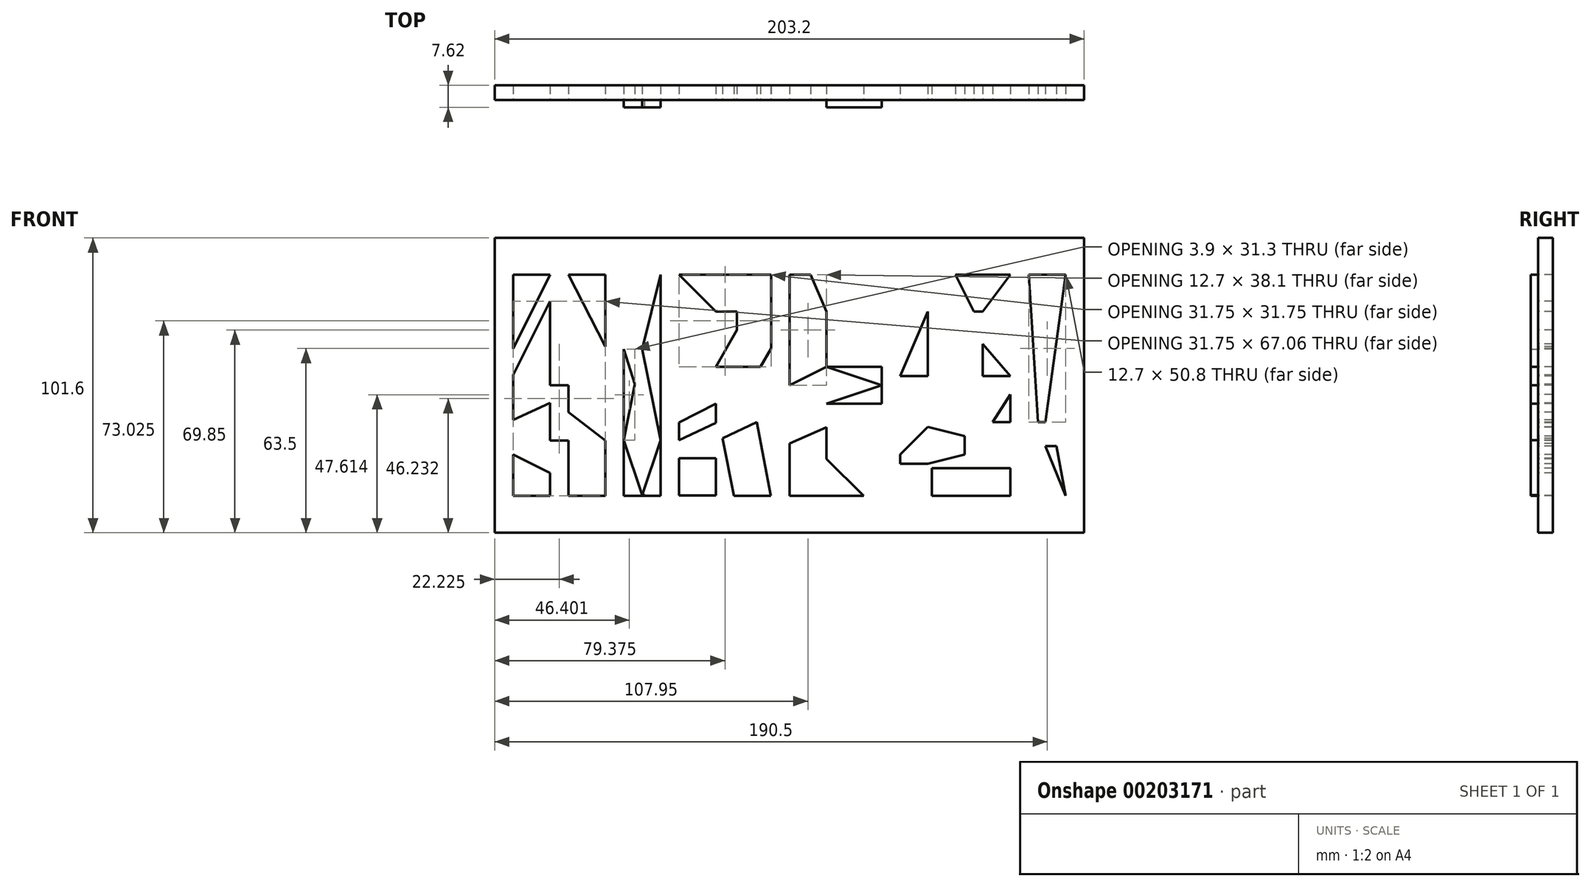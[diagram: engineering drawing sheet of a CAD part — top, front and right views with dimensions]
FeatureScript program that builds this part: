
annotation { "Feature Type Name" : "Feature", "Feature Type Description" : "" }
export const myFeature = defineFeature(function(context is Context, id is Id, definition is map)
    precondition{}
    {
        {
            var Q0;
            Q0=qCreatedBy(makeId("Front.planeOp"),FACE);
            var sketch = newSketch(context, id + "F0", { "sketchPlane" : qUnion([Q0])});
            skLineSegment(sketch, "E0.bottom", {"start": v(0, 0) * mm, "end": v(220.66, 0) * mm, "construction": true});
            skLineSegment(sketch, "E0.top", {"start": v(0, 138.11) * mm, "end": v(220.66, 138.11) * mm, "construction": true});
            skLineSegment(sketch, "E0.left", {"start": v(0, 0) * mm, "end": v(0, 138.11) * mm, "construction": true});
            skLineSegment(sketch, "E0.right", {"start": v(220.66, 0) * mm, "end": v(220.66, 138.11) * mm, "construction": true});
            skSolve(sketch);
        }
        {
            var Q0;
            Q0=qCreatedBy(makeId("Front.planeOp"),FACE);
            var sketch = newSketch(context, id + "F1", { "sketchPlane" : qUnion([Q0])});
            skLineSegment(sketch, "E1.bottom", {"start": v(0, 0) * mm, "end": v(203.2, 0) * mm});
            skLineSegment(sketch, "E1.top", {"start": v(0, 101.6) * mm, "end": v(203.2, 101.6) * mm});
            skLineSegment(sketch, "E1.left", {"start": v(0, 0) * mm, "end": v(0, 101.6) * mm});
            skLineSegment(sketch, "E1.right", {"start": v(203.2, 0) * mm, "end": v(203.2, 101.6) * mm});
            skSolve(sketch);
        }
        {
            var Q0;
            Q0=makeQuery(id+"F1.imprint","IMPRINT",FACE,{"disambiguationData":[TD([[makeQuery(id+"F1.imprint","IMPRINT",EDGE,{"derivedFrom":sQuery(id+"F1.wireOp",EDGE,"E1.bottom")}),1.0]])]});
            extrude(context, id + "F2", {"entities" : qUnion([Q0]), "oppositeDirection" : true, "depth" : 5.08 * mm});
        }
        {
            var Q0;
            Q0=makeQuery(id+"F2.opExtrude","CAP_FACE",FACE,{"disambiguationData":[OSD([sQuery(id+"F1.wireOp",EDGE,"E1.bottom"),sQuery(id+"F1.wireOp",EDGE,"E1.top"),sQuery(id+"F1.wireOp",EDGE,"E1.left"),sQuery(id+"F1.wireOp",EDGE,"E1.right")])],"isStart":true});
            var sketch = newSketch(context, id + "F3", { "sketchPlane" : qUnion([Q0])});
            skLineSegment(sketch, "E2", {"start": v(0, 50.8) * mm, "end": v(203.2, 50.8) * mm, "construction": true});
            skLineSegment(sketch, "E3", {"start": v(6.35, 88.9) * mm, "end": v(19.05, 88.9) * mm});
            skLineSegment(sketch, "E4", {"start": v(19.05, 88.9) * mm, "end": v(19.05, 50.8) * mm});
            skLineSegment(sketch, "E5", {"start": v(19.05, 50.8) * mm, "end": v(25.4, 50.8) * mm});
            skLineSegment(sketch, "E6", {"start": v(25.4, 50.8) * mm, "end": v(25.4, 88.9) * mm});
            skLineSegment(sketch, "E7", {"start": v(25.4, 88.9) * mm, "end": v(38.1, 88.9) * mm});
            skLineSegment(sketch, "E8", {"start": v(38.1, 88.9) * mm, "end": v(38.1, 50.8) * mm});
            skLineSegment(sketch, "E9", {"start": v(38.1, 50.8) * mm, "end": v(38.1, 12.7) * mm});
            skLineSegment(sketch, "E10", {"start": v(38.1, 12.7) * mm, "end": v(25.4, 12.7) * mm});
            skLineSegment(sketch, "E11", {"start": v(25.4, 12.7) * mm, "end": v(25.4, 31.75) * mm});
            skLineSegment(sketch, "E12", {"start": v(25.4, 31.75) * mm, "end": v(19.05, 31.75) * mm});
            skLineSegment(sketch, "E13", {"start": v(19.05, 31.75) * mm, "end": v(19.05, 12.7) * mm});
            skLineSegment(sketch, "E14", {"start": v(19.05, 12.7) * mm, "end": v(6.35, 12.7) * mm});
            skLineSegment(sketch, "E15", {"start": v(44.45, 88.9) * mm, "end": v(44.45, 12.7) * mm});
            skLineSegment(sketch, "E16", {"start": v(44.45, 12.7) * mm, "end": v(57.15, 12.7) * mm});
            skLineSegment(sketch, "E17", {"start": v(57.15, 12.7) * mm, "end": v(57.15, 88.9) * mm});
            skLineSegment(sketch, "E18", {"start": v(57.15, 88.9) * mm, "end": v(44.45, 88.9) * mm});
            skLineSegment(sketch, "E19", {"start": v(63.5, 88.9) * mm, "end": v(63.5, 12.7) * mm});
            skPoint(sketch, "E19.startSnap0", {"position": v(50.8, 88.9) * mm});
            skLineSegment(sketch, "E20", {"start": v(63.5, 12.7) * mm, "end": v(76.2, 12.7) * mm});
            skLineSegment(sketch, "E21", {"start": v(76.2, 12.7) * mm, "end": v(76.2, 44.45) * mm});
            skLineSegment(sketch, "E22", {"start": v(76.2, 44.45) * mm, "end": v(82.32, 12.7) * mm});
            skLineSegment(sketch, "E23", {"start": v(82.32, 12.7) * mm, "end": v(95.25, 12.7) * mm});
            skLineSegment(sketch, "E24", {"start": v(95.25, 12.7) * mm, "end": v(87.91, 50.8) * mm});
            skLineSegment(sketch, "E25", {"start": v(87.91, 50.8) * mm, "end": v(95.25, 63.5) * mm});
            skLineSegment(sketch, "E26", {"start": v(95.25, 63.5) * mm, "end": v(95.25, 88.9) * mm});
            skLineSegment(sketch, "E27", {"start": v(95.25, 88.9) * mm, "end": v(63.5, 88.9) * mm});
            skLineSegment(sketch, "E28", {"start": v(101.6, 88.9) * mm, "end": v(101.6, 12.7) * mm});
            skLineSegment(sketch, "E29", {"start": v(101.6, 12.7) * mm, "end": v(133.35, 12.7) * mm});
            skLineSegment(sketch, "E30", {"start": v(133.35, 12.7) * mm, "end": v(133.35, 25.4) * mm});
            skLineSegment(sketch, "E31", {"start": v(133.35, 25.4) * mm, "end": v(114.3, 25.4) * mm});
            skLineSegment(sketch, "E32", {"start": v(114.3, 25.4) * mm, "end": v(114.3, 44.45) * mm});
            skLineSegment(sketch, "E33", {"start": v(114.3, 44.45) * mm, "end": v(133.35, 44.45) * mm});
            skLineSegment(sketch, "E34", {"start": v(133.35, 44.45) * mm, "end": v(133.35, 57.15) * mm});
            skLineSegment(sketch, "E35", {"start": v(133.35, 57.15) * mm, "end": v(114.3, 57.15) * mm});
            skLineSegment(sketch, "E36", {"start": v(114.3, 57.15) * mm, "end": v(114.3, 76.2) * mm});
            skLineSegment(sketch, "E37", {"start": v(114.3, 76.2) * mm, "end": v(133.35, 76.2) * mm});
            skLineSegment(sketch, "E38", {"start": v(133.35, 76.2) * mm, "end": v(133.35, 88.9) * mm});
            skLineSegment(sketch, "E39", {"start": v(133.35, 88.9) * mm, "end": v(101.6, 88.9) * mm});
            skLineSegment(sketch, "E40", {"start": v(139.7, 88.9) * mm, "end": v(177.8, 88.9) * mm});
            skLineSegment(sketch, "E41", {"start": v(177.8, 88.9) * mm, "end": v(177.8, 53.98) * mm});
            skLineSegment(sketch, "E42", {"start": v(168.28, 53.98) * mm, "end": v(168.28, 76.2) * mm});
            skLineSegment(sketch, "E43", {"start": v(149.23, 76.2) * mm, "end": v(149.23, 53.98) * mm});
            skLineSegment(sketch, "E44", {"start": v(139.7, 12.7) * mm, "end": v(177.8, 12.7) * mm});
            skLineSegment(sketch, "E45", {"start": v(177.8, 12.7) * mm, "end": v(177.8, 22.23) * mm});
            skLineSegment(sketch, "E46", {"start": v(177.8, 22.23) * mm, "end": v(149.23, 22.23) * mm});
            skLineSegment(sketch, "E47", {"start": v(149.23, 22.23) * mm, "end": v(149.23, 23.81) * mm});
            skLineSegment(sketch, "E48", {"start": v(149.23, 36.51) * mm, "end": v(149.23, 38.1) * mm});
            skLineSegment(sketch, "E49", {"start": v(149.23, 38.1) * mm, "end": v(177.8, 38.1) * mm});
            skLineSegment(sketch, "E50", {"start": v(177.8, 38.1) * mm, "end": v(177.8, 47.63) * mm});
            skLineSegment(sketch, "E51", {"start": v(6.35, 88.9) * mm, "end": v(6.35, 12.7) * mm});
            skLineSegment(sketch, "E52", {"start": v(149.23, 76.2) * mm, "end": v(152.4, 76.2) * mm});
            skLineSegment(sketch, "E53", {"start": v(152.4, 76.2) * mm, "end": v(155.57, 63.5) * mm});
            skLineSegment(sketch, "E54", {"start": v(155.57, 63.5) * mm, "end": v(161.93, 63.5) * mm});
            skLineSegment(sketch, "E55", {"start": v(161.93, 63.5) * mm, "end": v(165.1, 76.2) * mm});
            skLineSegment(sketch, "E56", {"start": v(165.1, 76.2) * mm, "end": v(168.28, 76.2) * mm});
            skPoint(sketch, "E57", {"position": v(158.75, 88.9) * mm});
            skPoint(sketch, "E58", {"position": v(158.75, 63.5) * mm});
            skLineSegment(sketch, "E59", {"start": v(161.93, 33.34) * mm, "end": v(161.93, 26.99) * mm});
            skPoint(sketch, "E60", {"position": v(161.93, 30.16) * mm});
            skLineSegment(sketch, "E61", {"start": v(139.7, 88.9) * mm, "end": v(139.7, 53.98) * mm});
            skLineSegment(sketch, "E62", {"start": v(139.7, 53.98) * mm, "end": v(149.23, 53.98) * mm});
            skLineSegment(sketch, "E63", {"start": v(168.28, 53.98) * mm, "end": v(177.8, 53.98) * mm});
            skLineSegment(sketch, "E64", {"start": v(139.7, 47.63) * mm, "end": v(177.8, 47.63) * mm});
            skLineSegment(sketch, "E65", {"start": v(139.7, 47.63) * mm, "end": v(139.7, 12.7) * mm});
            skLineSegment(sketch, "E66", {"start": v(161.93, 33.34) * mm, "end": v(149.23, 36.51) * mm});
            skLineSegment(sketch, "E67", {"start": v(149.23, 23.81) * mm, "end": v(161.93, 26.99) * mm});
            skPoint(sketch, "E68", {"position": v(139.7, 30.16) * mm});
            skLineSegment(sketch, "E69", {"start": v(184.15, 88.9) * mm, "end": v(196.85, 88.9) * mm});
            skLineSegment(sketch, "E70", {"start": v(196.85, 88.9) * mm, "end": v(193.67, 38.1) * mm});
            skLineSegment(sketch, "E71", {"start": v(193.67, 38.1) * mm, "end": v(187.33, 38.1) * mm});
            skLineSegment(sketch, "E72", {"start": v(187.33, 38.1) * mm, "end": v(184.15, 88.9) * mm});
            skPoint(sketch, "E73", {"position": v(190.5, 88.9) * mm});
            skPoint(sketch, "E74", {"position": v(190.5, 38.1) * mm});
            skLineSegment(sketch, "E75", {"start": v(187.32, 29.85) * mm, "end": v(184.15, 12.7) * mm});
            skLineSegment(sketch, "E76", {"start": v(184.15, 12.7) * mm, "end": v(196.85, 12.7) * mm});
            skLineSegment(sketch, "E77", {"start": v(196.85, 12.7) * mm, "end": v(193.68, 29.85) * mm});
            skLineSegment(sketch, "E78", {"start": v(193.67, 29.85) * mm, "end": v(187.33, 29.85) * mm});
            skPoint(sketch, "E79", {"position": v(190.5, 29.85) * mm});
            skPoint(sketch, "E80", {"position": v(190.5, 12.7) * mm});
            skLineSegment(sketch, "E81", {"start": v(76.2, 57.15) * mm, "end": v(76.2, 76.2) * mm});
            skLineSegment(sketch, "E82", {"start": v(76.2, 76.2) * mm, "end": v(83.54, 76.2) * mm});
            skLineSegment(sketch, "E83", {"start": v(83.54, 76.2) * mm, "end": v(83.54, 69.85) * mm});
            skLineSegment(sketch, "E84", {"start": v(83.54, 69.85) * mm, "end": v(76.2, 57.15) * mm});
            skSolve(sketch);
        }
        {
            var Q0;
            Q0=makeQuery(id+"F3.imprint","IMPRINT",FACE,{"disambiguationData":[TD([[makeQuery(id+"F3.imprint","IMPRINT",EDGE,{"derivedFrom":sQuery(id+"F3.wireOp",EDGE,"E3")}),1.0]])]});
            var sketch = newSketch(context, id + "F4", { "sketchPlane" : qUnion([Q0])});
            skLineSegment(sketch, "E85", {"start": v(6.35, 63.49) * mm, "end": v(19.05, 88.9) * mm});
            skLineSegment(sketch, "E86", {"start": v(19.05, 88.9) * mm, "end": v(6.35, 88.9) * mm});
            skLineSegment(sketch, "E87", {"start": v(6.35, 88.9) * mm, "end": v(6.35, 63.49) * mm});
            skLineSegment(sketch, "E88", {"start": v(6.35, 54.35) * mm, "end": v(19.05, 79.76) * mm});
            skLineSegment(sketch, "E89", {"start": v(19.05, 79.76) * mm, "end": v(19.05, 50.8) * mm});
            skLineSegment(sketch, "E90", {"start": v(6.35, 38.97) * mm, "end": v(6.35, 54.35) * mm});
            skLineSegment(sketch, "E91", {"start": v(19.05, 31.75) * mm, "end": v(19.05, 44.79) * mm});
            skLineSegment(sketch, "E92", {"start": v(25.4, 41.55) * mm, "end": v(38.1, 31.75) * mm});
            skLineSegment(sketch, "E93", {"start": v(6.35, 26.94) * mm, "end": v(19.05, 20.6) * mm});
            skLineSegment(sketch, "E94", {"start": v(19.05, 20.6) * mm, "end": v(19.05, 12.7) * mm});
            skLineSegment(sketch, "E95", {"start": v(19.05, 12.7) * mm, "end": v(6.35, 12.7) * mm});
            skLineSegment(sketch, "E96", {"start": v(6.35, 12.7) * mm, "end": v(6.35, 26.94) * mm});
            skLineSegment(sketch, "E97", {"start": v(19.05, 50.8) * mm, "end": v(25.4, 50.8) * mm});
            skLineSegment(sketch, "E98", {"start": v(25.4, 50.8) * mm, "end": v(25.4, 41.55) * mm});
            skLineSegment(sketch, "E99", {"start": v(6.35, 38.97) * mm, "end": v(19.05, 44.79) * mm});
            skLineSegment(sketch, "E100", {"start": v(38.1, 31.75) * mm, "end": v(38.1, 12.7) * mm});
            skLineSegment(sketch, "E101", {"start": v(38.1, 12.7) * mm, "end": v(25.4, 12.7) * mm});
            skLineSegment(sketch, "E102", {"start": v(25.4, 12.7) * mm, "end": v(25.4, 31.75) * mm});
            skLineSegment(sketch, "E103", {"start": v(25.4, 31.75) * mm, "end": v(19.05, 31.75) * mm});
            skLineSegment(sketch, "E104", {"start": v(25.4, 64.16) * mm, "end": v(25.4, 88.9) * mm});
            skLineSegment(sketch, "E105", {"start": v(25.4, 88.9) * mm, "end": v(38.12, 64.16) * mm});
            skLineSegment(sketch, "E106", {"start": v(38.12, 64.16) * mm, "end": v(25.4, 64.16) * mm});
            skLineSegment(sketch, "E107", {"start": v(44.45, 88.9) * mm, "end": v(44.45, 63.26) * mm});
            skLineSegment(sketch, "E108", {"start": v(44.45, 63.26) * mm, "end": v(48.35, 51.2) * mm});
            skLineSegment(sketch, "E109", {"start": v(48.35, 51.2) * mm, "end": v(44.45, 31.96) * mm});
            skLineSegment(sketch, "E110", {"start": v(44.45, 31.96) * mm, "end": v(50.8, 12.7) * mm});
            skLineSegment(sketch, "E111", {"start": v(50.8, 12.7) * mm, "end": v(57.15, 31.96) * mm});
            skLineSegment(sketch, "E112", {"start": v(57.15, 31.96) * mm, "end": v(53.25, 51.2) * mm});
            skLineSegment(sketch, "E113", {"start": v(53.25, 51.2) * mm, "end": v(50.8, 63.26) * mm});
            skLineSegment(sketch, "E114", {"start": v(50.8, 63.26) * mm, "end": v(57.15, 88.9) * mm});
            skLineSegment(sketch, "E115", {"start": v(57.15, 88.9) * mm, "end": v(44.45, 88.9) * mm});
            skLineSegment(sketch, "E116", {"start": v(63.5, 88.9) * mm, "end": v(76.2, 76.2) * mm});
            skLineSegment(sketch, "E117", {"start": v(76.2, 76.2) * mm, "end": v(76.2, 57.15) * mm});
            skLineSegment(sketch, "E118", {"start": v(63.5, 38.08) * mm, "end": v(63.5, 88.9) * mm});
            skLineSegment(sketch, "E119", {"start": v(63.5, 25.77) * mm, "end": v(63.5, 31.96) * mm});
            skLineSegment(sketch, "E120", {"start": v(63.5, 31.96) * mm, "end": v(76.2, 37.86) * mm});
            skLineSegment(sketch, "E121", {"start": v(76.2, 37.86) * mm, "end": v(76.2, 25.77) * mm});
            skLineSegment(sketch, "E122", {"start": v(76.2, 25.77) * mm, "end": v(63.5, 25.77) * mm});
            skLineSegment(sketch, "E123", {"start": v(76.2, 57.15) * mm, "end": v(91.58, 57.15) * mm});
            skLineSegment(sketch, "E124", {"start": v(91.58, 57.15) * mm, "end": v(87.91, 50.8) * mm});
            skLineSegment(sketch, "E125", {"start": v(76.2, 44.45) * mm, "end": v(63.5, 38.08) * mm});
            skLineSegment(sketch, "E126", {"start": v(78.48, 32.6) * mm, "end": v(90.35, 38.12) * mm});
            skLineSegment(sketch, "E127", {"start": v(114.3, 57.15) * mm, "end": v(101.6, 50.8) * mm});
            skLineSegment(sketch, "E128", {"start": v(101.6, 50.8) * mm, "end": v(114.3, 44.45) * mm});
            skLineSegment(sketch, "E129", {"start": v(114.3, 44.45) * mm, "end": v(133.35, 50.8) * mm});
            skLineSegment(sketch, "E130", {"start": v(133.35, 50.8) * mm, "end": v(114.3, 57.15) * mm});
            skLineSegment(sketch, "E131", {"start": v(114.3, 36.42) * mm, "end": v(101.6, 30.85) * mm});
            skLineSegment(sketch, "E132", {"start": v(101.6, 30.85) * mm, "end": v(101.6, 12.7) * mm});
            skLineSegment(sketch, "E133", {"start": v(101.6, 12.7) * mm, "end": v(127.23, 12.7) * mm});
            skLineSegment(sketch, "E134", {"start": v(127.23, 12.7) * mm, "end": v(114.3, 25.4) * mm});
            skLineSegment(sketch, "E135", {"start": v(114.3, 25.4) * mm, "end": v(114.3, 36.42) * mm});
            skLineSegment(sketch, "E136", {"start": v(108.95, 88.9) * mm, "end": v(114.3, 76.2) * mm});
            skLineSegment(sketch, "E137", {"start": v(114.3, 76.2) * mm, "end": v(133.35, 76.2) * mm});
            skLineSegment(sketch, "E138", {"start": v(133.35, 76.2) * mm, "end": v(133.35, 88.9) * mm});
            skLineSegment(sketch, "E139", {"start": v(133.35, 88.9) * mm, "end": v(108.95, 88.9) * mm});
            skLineSegment(sketch, "E140", {"start": v(152.4, 76.2) * mm, "end": v(158.75, 88.9) * mm});
            skLineSegment(sketch, "E141", {"start": v(158.75, 88.9) * mm, "end": v(165.1, 76.2) * mm});
            skLineSegment(sketch, "E142", {"start": v(165.1, 76.2) * mm, "end": v(161.93, 63.5) * mm});
            skLineSegment(sketch, "E143", {"start": v(161.93, 63.5) * mm, "end": v(155.57, 63.5) * mm});
            skLineSegment(sketch, "E144", {"start": v(155.57, 63.5) * mm, "end": v(152.4, 76.2) * mm});
            skLineSegment(sketch, "E145", {"start": v(168.28, 76.2) * mm, "end": v(177.8, 88.9) * mm});
            skLineSegment(sketch, "E146", {"start": v(177.8, 88.9) * mm, "end": v(177.8, 53.98) * mm});
            skLineSegment(sketch, "E147", {"start": v(177.8, 53.97) * mm, "end": v(168.27, 65.09) * mm});
            skLineSegment(sketch, "E148", {"start": v(168.28, 65.09) * mm, "end": v(168.28, 76.2) * mm});
            skLineSegment(sketch, "E149", {"start": v(139.7, 53.98) * mm, "end": v(149.23, 53.98) * mm});
            skLineSegment(sketch, "E150", {"start": v(149.23, 53.98) * mm, "end": v(149.23, 76.2) * mm});
            skLineSegment(sketch, "E151", {"start": v(149.23, 76.2) * mm, "end": v(139.7, 53.98) * mm});
            skLineSegment(sketch, "E152", {"start": v(139.7, 47.63) * mm, "end": v(177.8, 47.63) * mm});
            skLineSegment(sketch, "E153", {"start": v(177.8, 47.63) * mm, "end": v(171.66, 38.1) * mm});
            skLineSegment(sketch, "E154", {"start": v(171.66, 38.1) * mm, "end": v(149.23, 38.1) * mm});
            skLineSegment(sketch, "E155", {"start": v(139.7, 47.63) * mm, "end": v(139.7, 26.99) * mm});
            skLineSegment(sketch, "E156", {"start": v(139.7, 26.99) * mm, "end": v(149.23, 36.51) * mm});
            skLineSegment(sketch, "E157", {"start": v(149.23, 36.51) * mm, "end": v(149.23, 38.1) * mm});
            skLineSegment(sketch, "E158", {"start": v(150.7, 22.23) * mm, "end": v(150.7, 12.7) * mm});
            skLineSegment(sketch, "E159", {"start": v(150.7, 12.7) * mm, "end": v(139.7, 12.7) * mm});
            skLineSegment(sketch, "E160", {"start": v(139.7, 12.7) * mm, "end": v(139.7, 23.81) * mm});
            skLineSegment(sketch, "E161", {"start": v(139.7, 23.81) * mm, "end": v(149.23, 23.81) * mm});
            skLineSegment(sketch, "E162", {"start": v(149.23, 23.81) * mm, "end": v(149.23, 22.23) * mm});
            skLineSegment(sketch, "E163", {"start": v(149.23, 22.23) * mm, "end": v(150.7, 22.23) * mm});
            skLineSegment(sketch, "E164", {"start": v(187.33, 38.1) * mm, "end": v(187.33, 88.9) * mm});
            skLineSegment(sketch, "E165", {"start": v(187.33, 88.9) * mm, "end": v(184.15, 88.9) * mm});
            skLineSegment(sketch, "E166", {"start": v(184.15, 88.9) * mm, "end": v(187.33, 38.1) * mm});
            skLineSegment(sketch, "E167", {"start": v(189.76, 29.85) * mm, "end": v(196.85, 12.7) * mm});
            skLineSegment(sketch, "E168", {"start": v(196.85, 12.7) * mm, "end": v(193.68, 29.85) * mm});
            skLineSegment(sketch, "E169", {"start": v(193.68, 29.85) * mm, "end": v(189.76, 29.85) * mm});
            skLineSegment(sketch, "E170", {"start": v(189.76, 38.1) * mm, "end": v(196.85, 88.9) * mm});
            skLineSegment(sketch, "E171", {"start": v(196.85, 88.9) * mm, "end": v(193.68, 38.1) * mm});
            skLineSegment(sketch, "E172", {"start": v(193.67, 38.1) * mm, "end": v(189.76, 38.1) * mm});
            skLineSegment(sketch, "E173", {"start": v(48.35, 51.2) * mm, "end": v(53.25, 51.2) * mm, "construction": true});
            skPoint(sketch, "E174", {"position": v(50.8, 51.2) * mm});
            skLineSegment(sketch, "E175", {"start": v(57.15, 88.9) * mm, "end": v(57.15, 31.96) * mm});
            skLineSegment(sketch, "E176", {"start": v(50.8, 12.7) * mm, "end": v(57.15, 12.7) * mm});
            skLineSegment(sketch, "E177", {"start": v(57.15, 12.7) * mm, "end": v(57.15, 31.96) * mm});
            skLineSegment(sketch, "E178", {"start": v(50.8, 12.7) * mm, "end": v(44.45, 12.7) * mm});
            skLineSegment(sketch, "E179", {"start": v(44.45, 12.7) * mm, "end": v(44.45, 31.96) * mm});
            skLineSegment(sketch, "E180", {"start": v(44.45, 63.26) * mm, "end": v(44.45, 31.96) * mm});
            skLineSegment(sketch, "E181", {"start": v(63.5, 88.9) * mm, "end": v(95.29, 88.9) * mm});
            skLineSegment(sketch, "E182", {"start": v(95.29, 88.9) * mm, "end": v(95.29, 63.17) * mm});
            skLineSegment(sketch, "E183", {"start": v(95.29, 63.17) * mm, "end": v(91.58, 57.15) * mm});
            skLineSegment(sketch, "E184", {"start": v(76.2, 57.15) * mm, "end": v(83.54, 69.85) * mm});
            skLineSegment(sketch, "E185", {"start": v(83.54, 69.85) * mm, "end": v(83.54, 76.2) * mm});
            skLineSegment(sketch, "E186", {"start": v(83.54, 76.2) * mm, "end": v(76.2, 76.2) * mm});
            skLineSegment(sketch, "E187", {"start": v(63.5, 38.08) * mm, "end": v(63.5, 31.96) * mm});
            skLineSegment(sketch, "E188", {"start": v(63.5, 25.77) * mm, "end": v(63.5, 12.87) * mm});
            skLineSegment(sketch, "E189", {"start": v(63.5, 12.87) * mm, "end": v(76.2, 12.87) * mm});
            skLineSegment(sketch, "E190", {"start": v(76.2, 12.87) * mm, "end": v(76.2, 25.77) * mm});
            skLineSegment(sketch, "E191", {"start": v(78.48, 32.6) * mm, "end": v(82.53, 12.66) * mm});
            skLineSegment(sketch, "E192", {"start": v(82.53, 12.66) * mm, "end": v(95.17, 12.66) * mm});
            skLineSegment(sketch, "E193", {"start": v(95.17, 12.66) * mm, "end": v(90.35, 38.12) * mm});
            skLineSegment(sketch, "E194", {"start": v(76.2, 44.45) * mm, "end": v(78.48, 32.6) * mm});
            skLineSegment(sketch, "E195", {"start": v(90.35, 38.12) * mm, "end": v(87.91, 50.8) * mm});
            skLineSegment(sketch, "E196", {"start": v(76.2, 37.86) * mm, "end": v(76.2, 44.45) * mm});
            skLineSegment(sketch, "E197", {"start": v(108.95, 88.9) * mm, "end": v(101.6, 88.9) * mm});
            skLineSegment(sketch, "E198", {"start": v(101.6, 88.9) * mm, "end": v(101.6, 50.8) * mm});
            skLineSegment(sketch, "E199", {"start": v(101.6, 50.8) * mm, "end": v(101.6, 30.85) * mm});
            skLineSegment(sketch, "E200", {"start": v(114.3, 36.42) * mm, "end": v(114.3, 44.45) * mm});
            skLineSegment(sketch, "E201", {"start": v(114.3, 44.45) * mm, "end": v(133.35, 44.45) * mm});
            skLineSegment(sketch, "E202", {"start": v(133.35, 44.45) * mm, "end": v(133.35, 50.8) * mm});
            skLineSegment(sketch, "E203", {"start": v(133.35, 50.8) * mm, "end": v(133.35, 57.15) * mm});
            skLineSegment(sketch, "E204", {"start": v(133.35, 57.15) * mm, "end": v(114.3, 57.15) * mm});
            skLineSegment(sketch, "E205", {"start": v(114.3, 57.15) * mm, "end": v(114.3, 76.2) * mm});
            skLineSegment(sketch, "E206", {"start": v(114.3, 25.4) * mm, "end": v(133.35, 25.4) * mm});
            skLineSegment(sketch, "E207", {"start": v(133.35, 25.4) * mm, "end": v(133.35, 12.76) * mm});
            skLineSegment(sketch, "E208", {"start": v(133.35, 12.76) * mm, "end": v(127.23, 12.7) * mm});
            skLineSegment(sketch, "E209", {"start": v(150.7, 12.7) * mm, "end": v(177.8, 12.7) * mm});
            skLineSegment(sketch, "E210", {"start": v(177.8, 12.7) * mm, "end": v(177.8, 22.23) * mm});
            skLineSegment(sketch, "E211", {"start": v(177.8, 22.23) * mm, "end": v(150.7, 22.23) * mm});
            skLineSegment(sketch, "E212", {"start": v(149.23, 23.81) * mm, "end": v(161.93, 26.99) * mm});
            skLineSegment(sketch, "E213", {"start": v(161.93, 33.34) * mm, "end": v(149.23, 36.51) * mm});
            skLineSegment(sketch, "E214", {"start": v(139.7, 23.81) * mm, "end": v(139.7, 26.99) * mm});
            skLineSegment(sketch, "E215", {"start": v(171.66, 38.1) * mm, "end": v(177.8, 38.1) * mm});
            skLineSegment(sketch, "E216", {"start": v(177.8, 38.1) * mm, "end": v(177.8, 47.63) * mm});
            skLineSegment(sketch, "E217", {"start": v(139.7, 53.98) * mm, "end": v(139.7, 88.9) * mm});
            skLineSegment(sketch, "E218", {"start": v(139.7, 88.9) * mm, "end": v(158.75, 88.9) * mm});
            skLineSegment(sketch, "E219", {"start": v(149.22, 76.2) * mm, "end": v(149.22, 76.2) * mm});
            skLineSegment(sketch, "E220", {"start": v(149.23, 76.2) * mm, "end": v(152.4, 76.2) * mm});
            skLineSegment(sketch, "E221", {"start": v(158.75, 88.9) * mm, "end": v(177.8, 88.9) * mm});
            skLineSegment(sketch, "E222", {"start": v(168.28, 76.2) * mm, "end": v(165.1, 76.2) * mm});
            skLineSegment(sketch, "E223", {"start": v(168.28, 65.09) * mm, "end": v(168.28, 53.98) * mm});
            skLineSegment(sketch, "E224", {"start": v(168.28, 53.98) * mm, "end": v(177.8, 53.98) * mm});
            skLineSegment(sketch, "E225", {"start": v(187.33, 88.9) * mm, "end": v(196.85, 88.9) * mm});
            skLineSegment(sketch, "E226", {"start": v(189.76, 38.1) * mm, "end": v(187.33, 38.1) * mm});
            skLineSegment(sketch, "E227", {"start": v(189.76, 29.85) * mm, "end": v(187.33, 29.85) * mm});
            skLineSegment(sketch, "E228", {"start": v(187.33, 29.85) * mm, "end": v(184.3, 12.7) * mm});
            skLineSegment(sketch, "E229", {"start": v(184.3, 12.7) * mm, "end": v(196.85, 12.7) * mm});
            skLineSegment(sketch, "E230", {"start": v(161.93, 26.99) * mm, "end": v(161.93, 33.34) * mm});
            skLineSegment(sketch, "E231", {"start": v(19.05, 20.6) * mm, "end": v(19.05, 31.75) * mm});
            skLineSegment(sketch, "E232", {"start": v(6.35, 38.97) * mm, "end": v(6.35, 26.94) * mm});
            skLineSegment(sketch, "E233", {"start": v(6.35, 54.35) * mm, "end": v(6.35, 63.49) * mm});
            skLineSegment(sketch, "E234", {"start": v(25.4, 88.9) * mm, "end": v(38.1, 88.9) * mm});
            skLineSegment(sketch, "E235", {"start": v(38.1, 88.9) * mm, "end": v(38.12, 64.16) * mm});
            skLineSegment(sketch, "E236", {"start": v(38.1, 31.75) * mm, "end": v(38.12, 64.16) * mm});
            skLineSegment(sketch, "E237", {"start": v(25.4, 50.8) * mm, "end": v(25.4, 64.16) * mm});
            skLineSegment(sketch, "E238", {"start": v(44.45, 31.96) * mm, "end": v(44.45, 12.7) * mm});
            skLineSegment(sketch, "E239", {"start": v(57.15, 31.96) * mm, "end": v(57.15, 12.7) * mm});
            skSolve(sketch);
        }
        {
            var Q0;
            {var subQ29=sQuery(id+"F4.wireOp",EDGE,"E86");Q0=makeQuery(id+"F4.imprint","IMPRINT",FACE,{"disambiguationData":[TD([[makeQuery(id+"F4.imprint","IMPRINT",EDGE,{"derivedFrom":subQ29}),1.0]])]});}
            var sketch = newSketch(context, id + "F5", { "sketchPlane" : qUnion([Q0])});
            skLineSegment(sketch, "E240", {"start": v(108.95, 88.9) * mm, "end": v(133.35, 88.9) * mm});
            skLineSegment(sketch, "E241", {"start": v(133.35, 88.9) * mm, "end": v(133.35, 76.2) * mm});
            skLineSegment(sketch, "E242", {"start": v(133.35, 76.2) * mm, "end": v(114.3, 76.2) * mm});
            skLineSegment(sketch, "E243", {"start": v(114.3, 76.2) * mm, "end": v(108.95, 88.9) * mm});
            skLineSegment(sketch, "E244", {"start": v(114.3, 57.15) * mm, "end": v(133.35, 50.8) * mm});
            skLineSegment(sketch, "E245", {"start": v(133.35, 50.8) * mm, "end": v(133.35, 57.15) * mm});
            skLineSegment(sketch, "E246", {"start": v(133.35, 57.15) * mm, "end": v(114.3, 57.15) * mm});
            skLineSegment(sketch, "E247", {"start": v(114.3, 44.45) * mm, "end": v(133.35, 44.45) * mm});
            skLineSegment(sketch, "E248", {"start": v(133.35, 44.45) * mm, "end": v(133.35, 50.8) * mm});
            skLineSegment(sketch, "E249", {"start": v(133.35, 50.8) * mm, "end": v(114.3, 44.45) * mm});
            skLineSegment(sketch, "E250", {"start": v(50.8, 63.26) * mm, "end": v(57.15, 88.9) * mm});
            skLineSegment(sketch, "E251", {"start": v(57.15, 88.9) * mm, "end": v(57.15, 31.96) * mm});
            skLineSegment(sketch, "E252", {"start": v(57.15, 31.96) * mm, "end": v(50.8, 63.26) * mm});
            skLineSegment(sketch, "E253", {"start": v(44.45, 12.7) * mm, "end": v(50.8, 12.7) * mm});
            skLineSegment(sketch, "E254", {"start": v(44.45, 31.96) * mm, "end": v(44.45, 12.7) * mm});
            skLineSegment(sketch, "E255", {"start": v(168.28, 65.09) * mm, "end": v(168.28, 53.98) * mm});
            skLineSegment(sketch, "E256", {"start": v(168.28, 53.98) * mm, "end": v(177.8, 53.98) * mm});
            skLineSegment(sketch, "E257", {"start": v(177.8, 53.97) * mm, "end": v(168.28, 65.09) * mm});
            skLineSegment(sketch, "E258", {"start": v(171.66, 38.1) * mm, "end": v(177.8, 38.1) * mm});
            skLineSegment(sketch, "E259", {"start": v(177.8, 38.1) * mm, "end": v(177.8, 47.63) * mm});
            skLineSegment(sketch, "E260", {"start": v(177.8, 47.63) * mm, "end": v(171.66, 38.1) * mm});
            skLineSegment(sketch, "E261", {"start": v(184.15, 88.9) * mm, "end": v(196.85, 88.9) * mm});
            skLineSegment(sketch, "E262", {"start": v(196.85, 88.9) * mm, "end": v(189.76, 38.1) * mm});
            skLineSegment(sketch, "E263", {"start": v(189.76, 38.1) * mm, "end": v(187.33, 38.1) * mm});
            skLineSegment(sketch, "E264", {"start": v(187.33, 38.1) * mm, "end": v(184.15, 88.9) * mm});
            skLineSegment(sketch, "E265", {"start": v(189.76, 29.84) * mm, "end": v(193.68, 29.85) * mm});
            skLineSegment(sketch, "E266", {"start": v(193.67, 29.85) * mm, "end": v(196.85, 12.7) * mm});
            skLineSegment(sketch, "E267", {"start": v(196.85, 12.7) * mm, "end": v(189.76, 29.85) * mm});
            skLineSegment(sketch, "E268", {"start": v(44.45, 31.96) * mm, "end": v(50.8, 12.95) * mm});
            skLineSegment(sketch, "E269", {"start": v(50.8, 12.95) * mm, "end": v(51.7, 12.95) * mm});
            skLineSegment(sketch, "E270", {"start": v(51.7, 12.95) * mm, "end": v(51.7, 12.7) * mm});
            skLineSegment(sketch, "E271", {"start": v(51.7, 12.7) * mm, "end": v(50.8, 12.7) * mm});
            skSolve(sketch);
        }
        {
            var Q0;
            Q0=makeQuery(id+"F4.imprint","IMPRINT",FACE,{"disambiguationData":[TD([[makeQuery(id+"F4.imprint","IMPRINT",EDGE,{"derivedFrom":sQuery(id+"F4.wireOp",EDGE,"E85")}),1.0]])]});
            var Q1;
            {var subQ0=sQuery(id+"F4.wireOp",EDGE,"E234");Q1=makeQuery(id+"F4.imprint","IMPRINT",FACE,{"disambiguationData":[TD([[makeQuery(id+"F4.imprint","IMPRINT",EDGE,{"derivedFrom":subQ0}),-1.0]])]});}
            var Q2;
            Q2=makeQuery(id+"F4.imprint","IMPRINT",FACE,{"disambiguationData":[TD([[makeQuery(id+"F4.imprint","IMPRINT",EDGE,{"derivedFrom":sQuery(id+"F4.wireOp",EDGE,"E88")}),-1.0]])]});
            var Q3;
            Q3=makeQuery(id+"F4.imprint","IMPRINT",FACE,{"disambiguationData":[TD([[makeQuery(id+"F4.imprint","IMPRINT",EDGE,{"derivedFrom":sQuery(id+"F4.wireOp",EDGE,"E93")}),-1.0]])]});
            var Q4;
            Q4=makeQuery(id+"F4.imprint","IMPRINT",FACE,{"disambiguationData":[TD([[makeQuery(id+"F4.imprint","IMPRINT",EDGE,{"derivedFrom":sQuery(id+"F4.wireOp",EDGE,"E108")}),-1.0]])]});
            var Q5;
            Q5=makeQuery(id+"F4.imprint","IMPRINT",FACE,{"disambiguationData":[TD([[makeQuery(id+"F4.imprint","IMPRINT",EDGE,{"derivedFrom":sQuery(id+"F4.wireOp",EDGE,"E111")}),-1.0]])]});
            var Q6;
            Q6=makeQuery(id+"F4.imprint","IMPRINT",FACE,{"disambiguationData":[TD([[makeQuery(id+"F4.imprint","IMPRINT",EDGE,{"derivedFrom":sQuery(id+"F4.wireOp",EDGE,"E122")}),1.0]])]});
            var Q7;
            {var subQ0=sQuery(id+"F4.wireOp",EDGE,"E126");Q7=makeQuery(id+"F4.imprint","IMPRINT",FACE,{"disambiguationData":[TD([[makeQuery(id+"F4.imprint","IMPRINT",EDGE,{"derivedFrom":subQ0}),-1.0]])]});}
            var Q8;
            Q8=makeQuery(id+"F4.imprint","IMPRINT",FACE,{"disambiguationData":[TD([[makeQuery(id+"F4.imprint","IMPRINT",EDGE,{"derivedFrom":sQuery(id+"F4.wireOp",EDGE,"E120")}),1.0]])]});
            var Q9;
            {var subQ2=sQuery(id+"F4.wireOp",EDGE,"E116");Q9=makeQuery(id+"F4.imprint","IMPRINT",FACE,{"disambiguationData":[TD([[makeQuery(id+"F4.imprint","IMPRINT",EDGE,{"derivedFrom":subQ2}),1.0]])]});}
            var Q10;
            Q10=makeQuery(id+"F4.imprint","IMPRINT",FACE,{"disambiguationData":[TD([[makeQuery(id+"F4.imprint","IMPRINT",EDGE,{"derivedFrom":sQuery(id+"F4.wireOp",EDGE,"E127")}),-1.0]])]});
            var Q11;
            Q11=makeQuery(id+"F4.imprint","IMPRINT",FACE,{"disambiguationData":[TD([[makeQuery(id+"F4.imprint","IMPRINT",EDGE,{"derivedFrom":sQuery(id+"F4.wireOp",EDGE,"E131")}),1.0]])]});
            var Q12;
            Q12=makeQuery(id+"F4.imprint","IMPRINT",FACE,{"disambiguationData":[TD([[makeQuery(id+"F4.imprint","IMPRINT",EDGE,{"derivedFrom":sQuery(id+"F4.wireOp",EDGE,"E149")}),1.0]])]});
            var Q13;
            Q13=makeQuery(id+"F4.imprint","IMPRINT",FACE,{"disambiguationData":[TD([[makeQuery(id+"F4.imprint","IMPRINT",EDGE,{"derivedFrom":sQuery(id+"F4.wireOp",EDGE,"E141")}),1.0]])]});
            var Q14;
            Q14=makeQuery(id+"F4.imprint","IMPRINT",FACE,{"disambiguationData":[TD([[makeQuery(id+"F4.imprint","IMPRINT",EDGE,{"derivedFrom":sQuery(id+"F4.wireOp",EDGE,"E156")}),-1.0]])]});
            var Q15;
            Q15=makeQuery(id+"F4.imprint","IMPRINT",FACE,{"disambiguationData":[TD([[makeQuery(id+"F4.imprint","IMPRINT",EDGE,{"derivedFrom":sQuery(id+"F4.wireOp",EDGE,"E158")}),1.0]])]});
            extrude(context, id + "F6", {"entities" : qUnion([Q0, Q1, Q2, Q3, Q4, Q5, Q6, Q7, Q8, Q9, Q10, Q11, Q12, Q13, Q14, Q15]), "operationType" : NewBodyOperationType.REMOVE, "oppositeDirection" : true, "depth" : 6.35 * mm});
        }
        {
            var Q0;
            Q0=makeQuery(id+"F4.imprint","IMPRINT",FACE,{"disambiguationData":[TD([[makeQuery(id+"F4.imprint","IMPRINT",EDGE,{"derivedFrom":sQuery(id+"F4.wireOp",EDGE,"E164")}),-1.0]])]});
            var Q1;
            Q1=makeQuery(id+"F4.imprint","IMPRINT",FACE,{"disambiguationData":[TD([[makeQuery(id+"F4.imprint","IMPRINT",EDGE,{"derivedFrom":sQuery(id+"F4.wireOp",EDGE,"E167")}),1.0]])]});
            var Q2;
            Q2=makeQuery(id+"F5.imprint","IMPRINT",FACE,{"disambiguationData":[TD([[makeQuery(id+"F5.imprint","IMPRINT",EDGE,{"derivedFrom":sQuery(id+"F5.wireOp",EDGE,"E255")}),-1.0]])]});
            var Q3;
            {var subQ0=sQuery(id+"F5.wireOp",EDGE,"E262");Q3=makeQuery(id+"F5.imprint","IMPRINT",FACE,{"disambiguationData":[TD([[makeQuery(id+"F5.imprint","IMPRINT",EDGE,{"derivedFrom":subQ0}),-1.0]])]});}
            var Q4;
            Q4=makeQuery(id+"F4.imprint","IMPRINT",FACE,{"disambiguationData":[TD([[makeQuery(id+"F4.imprint","IMPRINT",EDGE,{"derivedFrom":sQuery(id+"F4.wireOp",EDGE,"E153")}),1.0]])]});
            extrude(context, id + "F7", {"entities" : qUnion([Q0, Q1, Q2, Q3, Q4]), "operationType" : NewBodyOperationType.REMOVE, "oppositeDirection" : true, "depth" : 6.35 * mm});
        }
        {
            var Q0;
            Q0=makeQuery(id+"F5.imprint","IMPRINT",FACE,{"disambiguationData":[TD([[makeQuery(id+"F5.imprint","IMPRINT",EDGE,{"derivedFrom":sQuery(id+"F5.wireOp",EDGE,"E250")}),-1.0]])]});
            var Q1;
            Q1=makeQuery(id+"F5.imprint","IMPRINT",FACE,{"disambiguationData":[TD([[makeQuery(id+"F5.imprint","IMPRINT",EDGE,{"derivedFrom":sQuery(id+"F5.wireOp",EDGE,"E253")}),1.0]])]});
            var Q2;
            Q2=makeQuery(id+"F5.imprint","IMPRINT",FACE,{"disambiguationData":[TD([[makeQuery(id+"F5.imprint","IMPRINT",EDGE,{"derivedFrom":sQuery(id+"F5.wireOp",EDGE,"E244")}),1.0]])]});
            var Q3;
            Q3=makeQuery(id+"F5.imprint","IMPRINT",FACE,{"disambiguationData":[TD([[makeQuery(id+"F5.imprint","IMPRINT",EDGE,{"derivedFrom":sQuery(id+"F5.wireOp",EDGE,"E247")}),1.0]])]});
            extrude(context, id + "F8", {"entities" : qUnion([Q0, Q1, Q2, Q3]), "depth" : 2.54 * mm});
        }
    });
